# Revit family: Manifold Bracket Assy-JCI_Sapphire_Plus-(70 bar)Novec1230
name_source: partatom
category: Specialty Equipment
revit_build: Autodesk Revit 2017 (Build: 20171027_0315(x64)
units: mm (PartAtom-declared; Revit-internal decimal feet)

## family parameters
Always vertical = No
Cut with Voids When Loaded = No
OmniClass Number = 23.29.33.13.11
Part Type = Normal
Room Calculation Point = No
Round Connector Dimension = Use Diameter
Shared = No
Work Plane-Based = Yes

## types (4) — shared parameters
Date Modified = YYYY/MM/DD
Equipment Abbreviation = MBR
Equipment Number = XXX
Family Version = 1.0
Fire Suppression Agent = ''3M Novec'' 1230 Fire Protection Fluid
Length = 47.6 mm  [stored 0.156168 ft]
Manufacturer = Johnson Controls, Inc.
Material = JCI - Metal - Steel
Model Disclaimer = For More Information Contact JOHNSON CONTROLS
Operating Temperature = 122 °F
Product Documentation Link = http://www.sapphireplus.com
Product Material = JCI - Iron - Gray; JCI - Plastic - Red - Matte
Product Page URL = http://www.sapphireplus.com
URL = http://www.sapphireplus.com
Weight = 0.00 lbf
Width = 47.6 mm  [stored 0.156168 ft]
zero-valued in all types: Default Elevation

## per-type parameters (varying)
| type | Cantilever Bracket Length | Cantilever Bracket Length ref | Cantilever Bracket Profile Height | Description | Height | Model | Part Description | Part Number | Pipe Clamp Radius | Unistrut Channel Length |
| 150mm (6 in) Double Profile | 300 mm  [stored 0.984252 ft] | 460 mm  [stored 1.50919 ft] | 80 mm  [stored 0.262467 ft] | 150mm (6 in) Double Profile | 50 mm  [stored 0.164042 ft] | 311700001 | 150mm (6 in) Double Profile | 311700001 | 75 mm | 500 mm  [stored 1.64042 ft] |
| 80mm (3 in) | 300 mm  [stored 0.984252 ft] | 300 mm  [stored 0.984252 ft] | 40 mm  [stored 0.131234 ft] | 80mm(3in) Manifold Bracket Assembly | 41 mm  [stored 0.134514 ft] | 311.205.010 | 80mm(3in) Manifold Bracket Assembly | 311.205.010 | 40 mm  [stored 0.131234 ft] | 500 mm  [stored 1.64042 ft] |
| 65mm (2.5 in) | 200 mm  [stored 0.656168 ft] | 150 mm | 40 mm  [stored 0.131234 ft] | 65mm(2.5in) Manifold Bracket Assembly | 50 mm  [stored 0.164042 ft] | 311.205.015 | 65mm(2.5in) Manifold Bracket Assembly | 311.205.015 | 32.5 mm  [stored 0.106627 ft] | 400 mm  [stored 1.31234 ft] |
| 100mm (5 in) | 300 mm  [stored 0.984252 ft] | 300 mm  [stored 0.984252 ft] | 40 mm  [stored 0.131234 ft] | 100mm(5in) Manifold Bracket Assembly | 50 mm  [stored 0.164042 ft] | 311.205.011 | 100mm(5in) Manifold Bracket Assembly | 311.205.011 | 50 mm  [stored 0.164042 ft] | 500 mm  [stored 1.64042 ft] |

note: [stored X ft] marks values corroborated as IEEE doubles in the binary element streams (Revit-internal decimal feet)

## geometry (parser evidence)
native form markers: Sweep x5
no freeform markers — native parametric forms only
